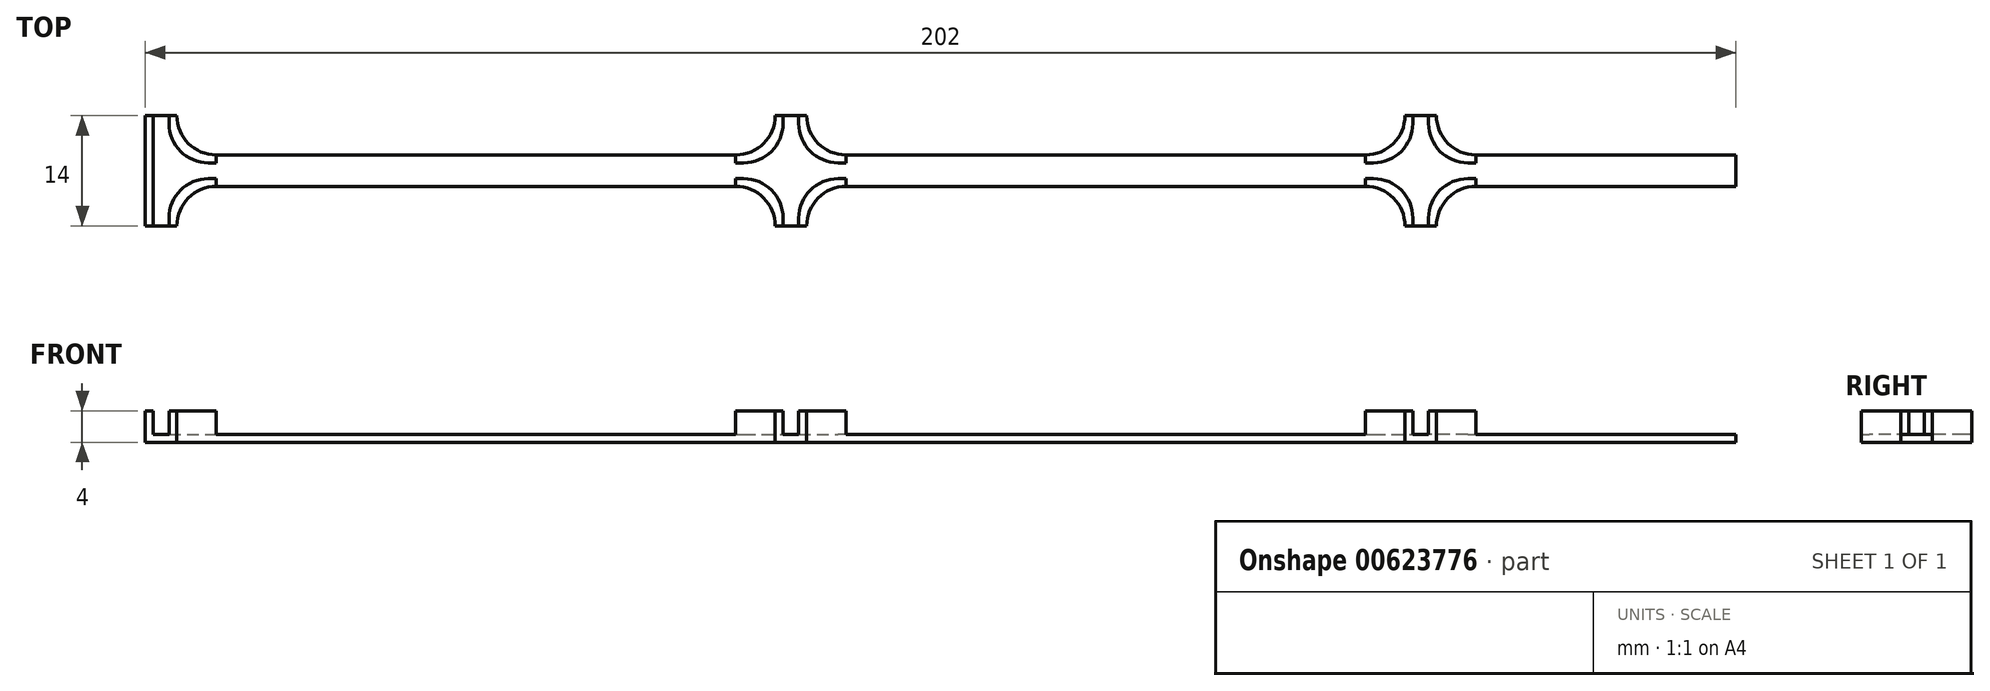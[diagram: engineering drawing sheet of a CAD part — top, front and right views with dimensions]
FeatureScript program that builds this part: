
annotation { "Feature Type Name" : "Feature", "Feature Type Description" : "" }
export const myFeature = defineFeature(function(context is Context, id is Id, definition is map)
    precondition{}
    {
        {
            var Q0;
            Q0=qCreatedBy(makeId("Top.planeOp"),FACE);
            var sketch = newSketch(context, id + "F0", { "sketchPlane" : qUnion([Q0])});
            skLineSegment(sketch, "E0.bottom", {"start": v(101, -2) * mm, "end": v(-101, -2) * mm});
            skLineSegment(sketch, "E0.top", {"start": v(101, 2) * mm, "end": v(-101, 2) * mm});
            skLineSegment(sketch, "E0.left", {"start": v(101, -2) * mm, "end": v(101, 2) * mm});
            skLineSegment(sketch, "E0.right", {"start": v(-101, -2) * mm, "end": v(-101, 2) * mm});
            skPoint(sketch, "E0.middle", {"position": v(0, 0) * mm});
            skLineSegment(sketch, "E1.bottom", {"start": v(-101, 7) * mm, "end": v(-97, 7) * mm});
            skLineSegment(sketch, "E1.top", {"start": v(-101, -7) * mm, "end": v(-97, -7) * mm});
            skLineSegment(sketch, "E1.left", {"start": v(-101, 7) * mm, "end": v(-101, -7) * mm});
            skLineSegment(sketch, "E1.right", {"start": v(-97, 7) * mm, "end": v(-97, -7) * mm});
            skLineSegment(sketch, "E2", {"start": v(-101, 0) * mm, "end": v(-101, 0) * mm});
            skLineSegment(sketch, "E3.bottom", {"start": v(-21, 7) * mm, "end": v(-17, 7) * mm});
            skLineSegment(sketch, "E3.top", {"start": v(-21, -7) * mm, "end": v(-17, -7) * mm});
            skLineSegment(sketch, "E3.left", {"start": v(-21, 7) * mm, "end": v(-21, -7) * mm});
            skLineSegment(sketch, "E3.right", {"start": v(-17, 7) * mm, "end": v(-17, -7) * mm});
            skPoint(sketch, "E3.middle", {"position": v(-19, 0) * mm});
            skLineSegment(sketch, "E4", {"start": v(-97, 4.56) * mm, "end": v(-17, 4.56) * mm});
            skLineSegment(sketch, "E5.bottom", {"start": v(63, 7) * mm, "end": v(59, 7) * mm});
            skLineSegment(sketch, "E5.top", {"start": v(63, -7) * mm, "end": v(59, -7) * mm});
            skLineSegment(sketch, "E5.left", {"start": v(63, 7) * mm, "end": v(63, -7) * mm});
            skLineSegment(sketch, "E5.right", {"start": v(59, 7) * mm, "end": v(59, -7) * mm});
            skPoint(sketch, "E5.middle", {"position": v(61, 0) * mm});
            skLineSegment(sketch, "E6", {"start": v(-17, 4.56) * mm, "end": v(63, 4.56) * mm});
            skSolve(sketch);
        }
        {
            var Q0;
            {var subQ3=sQuery(id+"F0.wireOp",EDGE,"E1.bottom");Q0=makeQuery(id+"F0.imprint","IMPRINT",FACE,{"disambiguationData":[TD([[makeQuery(id+"F0.imprint","IMPRINT",EDGE,{"derivedFrom":subQ3}),-1.0]])]});}
            var Q1;
            {var subQ0=sQuery(id+"F0.wireOp",EDGE,"E1.left");var subQ1=sQuery(id+"F0.wireOp",EDGE,"E0.bottom");var subQ2=makeQuery(id+"F0.imprint","INTERSECT",VERTEX,{"derivedFrom":[subQ1,subQ0]});Q1=makeQuery(id+"F0.imprint","IMPRINT",FACE,{"disambiguationData":[TD([[makeQuery(id+"F0.imprint","IMPRINT",EDGE,{"disambiguationData":[TD([[subQ2,1.0]])],"derivedFrom":subQ1}),-1.0]])]});}
            var Q2;
            {var subQ5=sQuery(id+"F0.wireOp",EDGE,"E1.top");Q2=makeQuery(id+"F0.imprint","IMPRINT",FACE,{"disambiguationData":[TD([[makeQuery(id+"F0.imprint","IMPRINT",EDGE,{"derivedFrom":subQ5}),1.0]])]});}
            var Q3;
            {var subQ0=sQuery(id+"F0.wireOp",EDGE,"E3.left");var subQ1=sQuery(id+"F0.wireOp",EDGE,"E0.bottom");var subQ2=makeQuery(id+"F0.imprint","INTERSECT",VERTEX,{"derivedFrom":[subQ1,subQ0]});Q3=makeQuery(id+"F0.imprint","IMPRINT",FACE,{"disambiguationData":[TD([[makeQuery(id+"F0.imprint","IMPRINT",EDGE,{"disambiguationData":[TD([[subQ2,-1.0]])],"derivedFrom":subQ1}),-1.0]])]});}
            var Q4;
            {var subQ0=sQuery(id+"F0.wireOp",EDGE,"E3.right");var subQ1=sQuery(id+"F0.wireOp",EDGE,"E0.top");var subQ2=makeQuery(id+"F0.imprint","INTERSECT",VERTEX,{"derivedFrom":[subQ1,subQ0]});Q4=makeQuery(id+"F0.imprint","IMPRINT",FACE,{"disambiguationData":[TD([[makeQuery(id+"F0.imprint","IMPRINT",EDGE,{"disambiguationData":[TD([[subQ2,-1.0]])],"derivedFrom":subQ1}),-1.0]])]});}
            var Q5;
            {var subQ0=sQuery(id+"F0.wireOp",EDGE,"E3.right");var subQ1=sQuery(id+"F0.wireOp",EDGE,"E0.bottom");var subQ2=makeQuery(id+"F0.imprint","INTERSECT",VERTEX,{"derivedFrom":[subQ1,subQ0]});Q5=makeQuery(id+"F0.imprint","IMPRINT",FACE,{"disambiguationData":[TD([[makeQuery(id+"F0.imprint","IMPRINT",EDGE,{"disambiguationData":[TD([[subQ2,-1.0]])],"derivedFrom":subQ1}),-1.0]])]});}
            var Q6;
            {var subQ5=sQuery(id+"F0.wireOp",EDGE,"E3.top");Q6=makeQuery(id+"F0.imprint","IMPRINT",FACE,{"disambiguationData":[TD([[makeQuery(id+"F0.imprint","IMPRINT",EDGE,{"derivedFrom":subQ5}),1.0]])]});}
            var Q7;
            {var subQ0=sQuery(id+"F0.wireOp",EDGE,"E3.bottom");Q7=makeQuery(id+"F0.imprint","IMPRINT",FACE,{"disambiguationData":[TD([[makeQuery(id+"F0.imprint","IMPRINT",EDGE,{"derivedFrom":subQ0}),-1.0]])]});}
            var Q8;
            {var subQ0=sQuery(id+"F0.wireOp",EDGE,"E5.right");var subQ1=sQuery(id+"F0.wireOp",EDGE,"E0.bottom");var subQ2=makeQuery(id+"F0.imprint","INTERSECT",VERTEX,{"derivedFrom":[subQ1,subQ0]});Q8=makeQuery(id+"F0.imprint","IMPRINT",FACE,{"disambiguationData":[TD([[makeQuery(id+"F0.imprint","IMPRINT",EDGE,{"disambiguationData":[TD([[subQ2,-1.0]])],"derivedFrom":subQ1}),-1.0]])]});}
            var Q9;
            {var subQ0=sQuery(id+"F0.wireOp",EDGE,"E5.bottom");Q9=makeQuery(id+"F0.imprint","IMPRINT",FACE,{"disambiguationData":[TD([[makeQuery(id+"F0.imprint","IMPRINT",EDGE,{"derivedFrom":subQ0}),1.0]])]});}
            var Q10;
            {var subQ0=sQuery(id+"F0.wireOp",EDGE,"E5.left");var subQ1=sQuery(id+"F0.wireOp",EDGE,"E0.top");var subQ2=makeQuery(id+"F0.imprint","INTERSECT",VERTEX,{"derivedFrom":[subQ1,subQ0]});Q10=makeQuery(id+"F0.imprint","IMPRINT",FACE,{"disambiguationData":[TD([[makeQuery(id+"F0.imprint","IMPRINT",EDGE,{"disambiguationData":[TD([[subQ2,-1.0]])],"derivedFrom":subQ1}),-1.0]])]});}
            var Q11;
            {var subQ5=sQuery(id+"F0.wireOp",EDGE,"E5.top");Q11=makeQuery(id+"F0.imprint","IMPRINT",FACE,{"disambiguationData":[TD([[makeQuery(id+"F0.imprint","IMPRINT",EDGE,{"derivedFrom":subQ5}),-1.0]])]});}
            var Q12;
            {var subQ0=sQuery(id+"F0.wireOp",EDGE,"E5.left");var subQ1=sQuery(id+"F0.wireOp",EDGE,"E0.bottom");var subQ2=makeQuery(id+"F0.imprint","INTERSECT",VERTEX,{"derivedFrom":[subQ1,subQ0]});Q12=makeQuery(id+"F0.imprint","IMPRINT",FACE,{"disambiguationData":[TD([[makeQuery(id+"F0.imprint","IMPRINT",EDGE,{"disambiguationData":[TD([[subQ2,-1.0]])],"derivedFrom":subQ1}),-1.0]])]});}
            var Q13;
            {var subQ0=sQuery(id+"F0.wireOp",EDGE,"E0.left");Q13=makeQuery(id+"F0.imprint","IMPRINT",FACE,{"disambiguationData":[TD([[makeQuery(id+"F0.imprint","IMPRINT",EDGE,{"derivedFrom":subQ0}),1.0]])]});}
            extrude(context, id + "F1", {"entities" : qUnion([Q0, Q1, Q2, Q3, Q4, Q5, Q6, Q7, Q8, Q9, Q10, Q11, Q12, Q13]), "depth" : 1 * mm, "offsetDistance" : 25 * mm});
        }
        {
            var Q0;
            Q0=makeQuery(id+"F1.opExtrude","CAP_FACE",FACE,{"disambiguationData":[OSD([sQuery(id+"F0.wireOp",EDGE,"E0.bottom"),sQuery(id+"F0.wireOp",EDGE,"E0.top"),sQuery(id+"F0.wireOp",EDGE,"E0.left"),sQuery(id+"F0.wireOp",EDGE,"E1.bottom"),sQuery(id+"F0.wireOp",EDGE,"E1.top"),sQuery(id+"F0.wireOp",EDGE,"E1.left"),sQuery(id+"F0.wireOp",EDGE,"E1.right"),sQuery(id+"F0.wireOp",EDGE,"E3.bottom"),sQuery(id+"F0.wireOp",EDGE,"E3.top"),sQuery(id+"F0.wireOp",EDGE,"E3.left"),sQuery(id+"F0.wireOp",EDGE,"E3.right"),sQuery(id+"F0.wireOp",EDGE,"E5.bottom"),sQuery(id+"F0.wireOp",EDGE,"E5.top"),sQuery(id+"F0.wireOp",EDGE,"E5.left"),sQuery(id+"F0.wireOp",EDGE,"E5.right")])],"isStart":false});
            var sketch = newSketch(context, id + "F2", { "sketchPlane" : qUnion([Q0])});
            skLineSegment(sketch, "E7.bottom", {"start": v(-101, 7) * mm, "end": v(-100, 7) * mm});
            skLineSegment(sketch, "E7.top", {"start": v(-101, -7) * mm, "end": v(-100, -7) * mm});
            skLineSegment(sketch, "E7.left", {"start": v(-101, 7) * mm, "end": v(-101, -7) * mm});
            skLineSegment(sketch, "E7.right", {"start": v(-100, 7) * mm, "end": v(-100, -7) * mm});
            skLineSegment(sketch, "E8.bottom", {"start": v(-97, 2) * mm, "end": v(-98, 2) * mm});
            skLineSegment(sketch, "E8.top", {"start": v(-97, 7) * mm, "end": v(-98, 7) * mm});
            skLineSegment(sketch, "E8.left", {"start": v(-97, 2) * mm, "end": v(-97, 7) * mm});
            skLineSegment(sketch, "E8.right", {"start": v(-98, 2) * mm, "end": v(-98, 7) * mm});
            skLineSegment(sketch, "E9.bottom", {"start": v(-97, -2) * mm, "end": v(-98, -2) * mm});
            skLineSegment(sketch, "E9.top", {"start": v(-97, -7) * mm, "end": v(-98, -7) * mm});
            skLineSegment(sketch, "E9.left", {"start": v(-97, -2) * mm, "end": v(-97, -7) * mm});
            skLineSegment(sketch, "E9.right", {"start": v(-98, -2) * mm, "end": v(-98, -7) * mm});
            skLineSegment(sketch, "E10.bottom", {"start": v(-98, -2) * mm, "end": v(-92, -2) * mm});
            skLineSegment(sketch, "E10.top", {"start": v(-98, -1) * mm, "end": v(-92, -1) * mm});
            skLineSegment(sketch, "E10.left", {"start": v(-98, -2) * mm, "end": v(-98, -1) * mm});
            skLineSegment(sketch, "E10.right", {"start": v(-92, -2) * mm, "end": v(-92, -1) * mm});
            skPoint(sketch, "E11.oppositeSnap0", {"position": v(-92, -1.5) * mm});
            skLineSegment(sketch, "E11.bottom", {"start": v(-98, 2) * mm, "end": v(-92, 2) * mm});
            skLineSegment(sketch, "E11.top", {"start": v(-98, 1) * mm, "end": v(-92, 1) * mm});
            skLineSegment(sketch, "E11.left", {"start": v(-98, 2) * mm, "end": v(-98, 1) * mm});
            skLineSegment(sketch, "E11.right", {"start": v(-92, 2) * mm, "end": v(-92, 1) * mm});
            skLineSegment(sketch, "E12.bottom", {"start": v(-21, 7) * mm, "end": v(-20, 7) * mm});
            skLineSegment(sketch, "E12.top", {"start": v(-21, 1) * mm, "end": v(-20, 1) * mm});
            skLineSegment(sketch, "E12.left", {"start": v(-21, 7) * mm, "end": v(-21, 1) * mm});
            skLineSegment(sketch, "E12.right", {"start": v(-20, 7) * mm, "end": v(-20, 1) * mm});
            skPoint(sketch, "E13.oppositeSnap0", {"position": v(-20.5, 1) * mm});
            skLineSegment(sketch, "E13.bottom", {"start": v(-17, 7) * mm, "end": v(-18, 7) * mm});
            skLineSegment(sketch, "E13.top", {"start": v(-17, 1) * mm, "end": v(-18, 1) * mm});
            skLineSegment(sketch, "E13.left", {"start": v(-17, 7) * mm, "end": v(-17, 1) * mm});
            skLineSegment(sketch, "E13.right", {"start": v(-18, 7) * mm, "end": v(-18, 1) * mm});
            skLineSegment(sketch, "E14.bottom", {"start": v(-17, 1) * mm, "end": v(-12, 1) * mm});
            skLineSegment(sketch, "E14.top", {"start": v(-17, 2) * mm, "end": v(-12, 2) * mm});
            skLineSegment(sketch, "E14.left", {"start": v(-17, 1) * mm, "end": v(-17, 2) * mm});
            skLineSegment(sketch, "E14.right", {"start": v(-12, 1) * mm, "end": v(-12, 2) * mm});
            skPoint(sketch, "E15.oppositeSnap0", {"position": v(-12, 1.5) * mm});
            skLineSegment(sketch, "E15.bottom", {"start": v(-17, -2) * mm, "end": v(-12, -2) * mm});
            skLineSegment(sketch, "E15.top", {"start": v(-17, -1) * mm, "end": v(-12, -1) * mm});
            skLineSegment(sketch, "E15.left", {"start": v(-17, -2) * mm, "end": v(-17, -1) * mm});
            skLineSegment(sketch, "E15.right", {"start": v(-12, -2) * mm, "end": v(-12, -1) * mm});
            skLineSegment(sketch, "E16.bottom", {"start": v(-17, -1) * mm, "end": v(-18, -1) * mm});
            skLineSegment(sketch, "E16.top", {"start": v(-17, -7) * mm, "end": v(-18, -7) * mm});
            skLineSegment(sketch, "E16.left", {"start": v(-17, -1) * mm, "end": v(-17, -7) * mm});
            skLineSegment(sketch, "E16.right", {"start": v(-18, -1) * mm, "end": v(-18, -7) * mm});
            skLineSegment(sketch, "E17.bottom", {"start": v(-21, -2) * mm, "end": v(-26, -2) * mm});
            skLineSegment(sketch, "E17.top", {"start": v(-21, -1) * mm, "end": v(-26, -1) * mm});
            skLineSegment(sketch, "E17.left", {"start": v(-21, -2) * mm, "end": v(-21, -1) * mm});
            skLineSegment(sketch, "E17.right", {"start": v(-26, -2) * mm, "end": v(-26, -1) * mm});
            skLineSegment(sketch, "E18.bottom", {"start": v(-21, -1) * mm, "end": v(-20, -1) * mm});
            skLineSegment(sketch, "E18.top", {"start": v(-21, -7) * mm, "end": v(-20, -7) * mm});
            skLineSegment(sketch, "E18.left", {"start": v(-21, -1) * mm, "end": v(-21, -7) * mm});
            skLineSegment(sketch, "E18.right", {"start": v(-20, -1) * mm, "end": v(-20, -7) * mm});
            skPoint(sketch, "E19.oppositeSnap0", {"position": v(-26, -1.5) * mm});
            skLineSegment(sketch, "E19.bottom", {"start": v(-21, 2) * mm, "end": v(-26, 2) * mm});
            skLineSegment(sketch, "E19.top", {"start": v(-21, 1) * mm, "end": v(-26, 1) * mm});
            skLineSegment(sketch, "E19.left", {"start": v(-21, 2) * mm, "end": v(-21, 1) * mm});
            skLineSegment(sketch, "E19.right", {"start": v(-26, 2) * mm, "end": v(-26, 1) * mm});
            skLineSegment(sketch, "E20.bottom", {"start": v(59, 7) * mm, "end": v(60, 7) * mm});
            skLineSegment(sketch, "E20.top", {"start": v(59, 1) * mm, "end": v(60, 1) * mm});
            skLineSegment(sketch, "E20.left", {"start": v(59, 7) * mm, "end": v(59, 1) * mm});
            skLineSegment(sketch, "E20.right", {"start": v(60, 7) * mm, "end": v(60, 1) * mm});
            skLineSegment(sketch, "E21.bottom", {"start": v(63, 7) * mm, "end": v(62, 7) * mm});
            skLineSegment(sketch, "E21.top", {"start": v(63, 1) * mm, "end": v(62, 1) * mm});
            skLineSegment(sketch, "E21.left", {"start": v(63, 7) * mm, "end": v(63, 1) * mm});
            skLineSegment(sketch, "E21.right", {"start": v(62, 7) * mm, "end": v(62, 1) * mm});
            skLineSegment(sketch, "E22.bottom", {"start": v(59, -7) * mm, "end": v(60, -7) * mm});
            skLineSegment(sketch, "E22.top", {"start": v(59, -1) * mm, "end": v(60, -1) * mm});
            skLineSegment(sketch, "E22.left", {"start": v(59, -7) * mm, "end": v(59, -1) * mm});
            skLineSegment(sketch, "E22.right", {"start": v(60, -7) * mm, "end": v(60, -1) * mm});
            skLineSegment(sketch, "E23.bottom", {"start": v(63, -7) * mm, "end": v(62, -7) * mm});
            skLineSegment(sketch, "E23.top", {"start": v(63, -1) * mm, "end": v(62, -1) * mm});
            skLineSegment(sketch, "E23.left", {"start": v(63, -7) * mm, "end": v(63, -1) * mm});
            skLineSegment(sketch, "E23.right", {"start": v(62, -7) * mm, "end": v(62, -1) * mm});
            skLineSegment(sketch, "E24.bottom", {"start": v(63, -1) * mm, "end": v(68, -1) * mm});
            skLineSegment(sketch, "E24.top", {"start": v(63, -2) * mm, "end": v(68, -2) * mm});
            skLineSegment(sketch, "E24.left", {"start": v(63, -1) * mm, "end": v(63, -2) * mm});
            skLineSegment(sketch, "E24.right", {"start": v(68, -1) * mm, "end": v(68, -2) * mm});
            skLineSegment(sketch, "E25.bottom", {"start": v(63, 1) * mm, "end": v(68, 1) * mm});
            skLineSegment(sketch, "E25.top", {"start": v(63, 2) * mm, "end": v(68, 2) * mm});
            skLineSegment(sketch, "E25.left", {"start": v(63, 1) * mm, "end": v(63, 2) * mm});
            skLineSegment(sketch, "E25.right", {"start": v(68, 1) * mm, "end": v(68, 2) * mm});
            skLineSegment(sketch, "E26.bottom", {"start": v(59, -1) * mm, "end": v(54, -1) * mm});
            skLineSegment(sketch, "E26.top", {"start": v(59, -2) * mm, "end": v(54, -2) * mm});
            skLineSegment(sketch, "E26.left", {"start": v(59, -1) * mm, "end": v(59, -2) * mm});
            skLineSegment(sketch, "E26.right", {"start": v(54, -1) * mm, "end": v(54, -2) * mm});
            skLineSegment(sketch, "E27.bottom", {"start": v(59, 1) * mm, "end": v(54, 1) * mm});
            skLineSegment(sketch, "E27.top", {"start": v(59, 2) * mm, "end": v(54, 2) * mm});
            skLineSegment(sketch, "E27.left", {"start": v(59, 1) * mm, "end": v(59, 2) * mm});
            skLineSegment(sketch, "E27.right", {"start": v(54, 1) * mm, "end": v(54, 2) * mm});
            skSolve(sketch);
        }
        {
            var Q0;
            Q0=makeQuery(id+"F2.imprint","IMPRINT",FACE,{"disambiguationData":[TD([[makeQuery(id+"F2.imprint","IMPRINT",EDGE,{"derivedFrom":sQuery(id+"F2.wireOp",EDGE,"E7.bottom")}),-1.0]])]});
            var Q1;
            Q1=makeQuery(id+"F2.imprint","IMPRINT",FACE,{"disambiguationData":[TD([[makeQuery(id+"F2.imprint","IMPRINT",EDGE,{"derivedFrom":sQuery(id+"F2.wireOp",EDGE,"E8.top")}),-1.0]])]});
            var Q2;
            Q2=makeQuery(id+"F2.imprint","IMPRINT",FACE,{"disambiguationData":[TD([[makeQuery(id+"F2.imprint","IMPRINT",EDGE,{"derivedFrom":sQuery(id+"F2.wireOp",EDGE,"E11.top")}),1.0]])]});
            var Q3;
            Q3=makeQuery(id+"F2.imprint","IMPRINT",FACE,{"disambiguationData":[TD([[makeQuery(id+"F2.imprint","IMPRINT",EDGE,{"derivedFrom":sQuery(id+"F2.wireOp",EDGE,"E10.top")}),-1.0]])]});
            var Q4;
            Q4=makeQuery(id+"F2.imprint","IMPRINT",FACE,{"disambiguationData":[TD([[makeQuery(id+"F2.imprint","IMPRINT",EDGE,{"derivedFrom":sQuery(id+"F2.wireOp",EDGE,"E9.top")}),1.0]])]});
            extrude(context, id + "F3", {"entities" : qUnion([Q0, Q1, Q2, Q3, Q4]), "operationType" : NewBodyOperationType.ADD, "depth" : 3 * mm, "offsetDistance" : 25 * mm});
        }
        {
            var Q0;
            Q0=makeQuery(id+"F3.boolean.opBoolean","MERGE",EDGE,{"derivedFrom":[makeQuery(id+"F1.opExtrude","SWEPT_EDGE",EDGE,{"disambiguationData":[OSD([sQuery(id+"F0.wireOp",EDGE,"E0.bottom"),sQuery(id+"F0.wireOp",EDGE,"E1.right")])]}),makeQuery(id+"F3.opExtrude","SWEPT_EDGE",EDGE,{"disambiguationData":[OSD([sQuery(id+"F2.wireOp",EDGE,"E9.left"),sQuery(id+"F2.wireOp",EDGE,"E10.bottom")])]})]});
            var Q1;
            Q1=makeQuery(id+"F3.opExtrude","SWEPT_EDGE",EDGE,{"disambiguationData":[OSD([sQuery(id+"F2.wireOp",EDGE,"E11.top"),sQuery(id+"F2.wireOp",EDGE,"E11.left")])]});
            var Q2;
            Q2=makeQuery(id+"F3.opExtrude","SWEPT_EDGE",EDGE,{"disambiguationData":[OSD([sQuery(id+"F2.wireOp",EDGE,"E10.top"),sQuery(id+"F2.wireOp",EDGE,"E10.left")])]});
            var Q3;
            Q3=makeQuery(id+"F3.boolean.opBoolean","MERGE",EDGE,{"derivedFrom":[makeQuery(id+"F1.opExtrude","SWEPT_EDGE",EDGE,{"disambiguationData":[OSD([sQuery(id+"F0.wireOp",EDGE,"E0.top"),sQuery(id+"F0.wireOp",EDGE,"E1.right")])]}),makeQuery(id+"F3.opExtrude","SWEPT_EDGE",EDGE,{"disambiguationData":[OSD([sQuery(id+"F2.wireOp",EDGE,"E8.left"),sQuery(id+"F2.wireOp",EDGE,"E11.bottom")])]})]});
            fillet(context, id + "F4", {"entities" : qUnion([Q0, Q1, Q2, Q3]), "radius" : 5 * mm, "tangentPropagation" : true, "allowEdgeOverflow" : false});
        }
        {
            var Q0;
            Q0=makeQuery(id+"F2.imprint","IMPRINT",FACE,{"disambiguationData":[TD([[makeQuery(id+"F2.imprint","IMPRINT",EDGE,{"derivedFrom":sQuery(id+"F2.wireOp",EDGE,"E12.bottom")}),-1.0]])]});
            var Q1;
            Q1=makeQuery(id+"F2.imprint","IMPRINT",FACE,{"disambiguationData":[TD([[makeQuery(id+"F2.imprint","IMPRINT",EDGE,{"derivedFrom":sQuery(id+"F2.wireOp",EDGE,"E13.bottom")}),-1.0]])]});
            var Q2;
            Q2=makeQuery(id+"F2.imprint","IMPRINT",FACE,{"disambiguationData":[TD([[makeQuery(id+"F2.imprint","IMPRINT",EDGE,{"derivedFrom":sQuery(id+"F2.wireOp",EDGE,"E14.bottom")}),1.0]])]});
            var Q3;
            Q3=makeQuery(id+"F2.imprint","IMPRINT",FACE,{"disambiguationData":[TD([[makeQuery(id+"F2.imprint","IMPRINT",EDGE,{"derivedFrom":sQuery(id+"F2.wireOp",EDGE,"E19.bottom")}),1.0]])]});
            var Q4;
            {var subQ0=sQuery(id+"F2.wireOp",EDGE,"E17.bottom");Q4=makeQuery(id+"F2.imprint","IMPRINT",FACE,{"disambiguationData":[TD([[makeQuery(id+"F2.imprint","IMPRINT",EDGE,{"derivedFrom":subQ0}),-1.0]])]});}
            var Q5;
            {var subQ3=sQuery(id+"F2.wireOp",EDGE,"E18.bottom");Q5=makeQuery(id+"F2.imprint","IMPRINT",FACE,{"disambiguationData":[TD([[makeQuery(id+"F2.imprint","IMPRINT",EDGE,{"derivedFrom":subQ3}),-1.0]])]});}
            var Q6;
            {var subQ0=sQuery(id+"F2.wireOp",EDGE,"E15.bottom");Q6=makeQuery(id+"F2.imprint","IMPRINT",FACE,{"disambiguationData":[TD([[makeQuery(id+"F2.imprint","IMPRINT",EDGE,{"derivedFrom":subQ0}),-1.0]])]});}
            var Q7;
            {var subQ3=sQuery(id+"F2.wireOp",EDGE,"E16.bottom");Q7=makeQuery(id+"F2.imprint","IMPRINT",FACE,{"disambiguationData":[TD([[makeQuery(id+"F2.imprint","IMPRINT",EDGE,{"derivedFrom":subQ3}),1.0]])]});}
            extrude(context, id + "F5", {"entities" : qUnion([Q0, Q1, Q2, Q3, Q4, Q5, Q6, Q7]), "operationType" : NewBodyOperationType.ADD, "depth" : 3 * mm, "offsetDistance" : 25 * mm});
        }
        {
            var Q0;
            Q0=makeQuery(id+"F5.opExtrude","SWEPT_EDGE",EDGE,{"disambiguationData":[OSD([sQuery(id+"F2.wireOp",EDGE,"E13.top"),sQuery(id+"F2.wireOp",EDGE,"E13.right")])]});
            var Q1;
            Q1=makeQuery(id+"F5.opExtrude","SWEPT_EDGE",EDGE,{"disambiguationData":[OSD([sQuery(id+"F2.wireOp",EDGE,"E12.top"),sQuery(id+"F2.wireOp",EDGE,"E12.right")])]});
            var Q2;
            Q2=makeQuery(id+"F5.boolean.opBoolean","MERGE",EDGE,{"derivedFrom":[makeQuery(id+"F1.opExtrude","SWEPT_EDGE",EDGE,{"disambiguationData":[OSD([sQuery(id+"F0.wireOp",EDGE,"E0.bottom"),sQuery(id+"F0.wireOp",EDGE,"E3.right")])]}),makeQuery(id+"F5.opExtrude","SWEPT_EDGE",EDGE,{"disambiguationData":[OSD([sQuery(id+"F2.wireOp",EDGE,"E15.bottom"),sQuery(id+"F2.wireOp",EDGE,"E16.left")])]})]});
            var Q3;
            Q3=makeQuery(id+"F5.opExtrude","SWEPT_EDGE",EDGE,{"disambiguationData":[OSD([sQuery(id+"F2.wireOp",EDGE,"E18.bottom"),sQuery(id+"F2.wireOp",EDGE,"E18.right")])]});
            var Q4;
            Q4=makeQuery(id+"F5.boolean.opBoolean","MERGE",EDGE,{"derivedFrom":[makeQuery(id+"F1.opExtrude","SWEPT_EDGE",EDGE,{"disambiguationData":[OSD([sQuery(id+"F0.wireOp",EDGE,"E0.bottom"),sQuery(id+"F0.wireOp",EDGE,"E3.left")])]}),makeQuery(id+"F5.opExtrude","SWEPT_EDGE",EDGE,{"disambiguationData":[OSD([sQuery(id+"F2.wireOp",EDGE,"E17.bottom"),sQuery(id+"F2.wireOp",EDGE,"E18.left")])]})]});
            var Q5;
            Q5=makeQuery(id+"F5.boolean.opBoolean","MERGE",EDGE,{"derivedFrom":[makeQuery(id+"F1.opExtrude","SWEPT_EDGE",EDGE,{"disambiguationData":[OSD([sQuery(id+"F0.wireOp",EDGE,"E0.top"),sQuery(id+"F0.wireOp",EDGE,"E3.left")])]}),makeQuery(id+"F5.opExtrude","SWEPT_EDGE",EDGE,{"disambiguationData":[OSD([sQuery(id+"F2.wireOp",EDGE,"E12.left"),sQuery(id+"F2.wireOp",EDGE,"E19.bottom"),sQuery(id+"F2.wireOp",EDGE,"E19.left")])]})]});
            var Q6;
            Q6=makeQuery(id+"F5.boolean.opBoolean","MERGE",EDGE,{"derivedFrom":[makeQuery(id+"F1.opExtrude","SWEPT_EDGE",EDGE,{"disambiguationData":[OSD([sQuery(id+"F0.wireOp",EDGE,"E0.top"),sQuery(id+"F0.wireOp",EDGE,"E3.right")])]}),makeQuery(id+"F5.opExtrude","SWEPT_EDGE",EDGE,{"disambiguationData":[OSD([sQuery(id+"F2.wireOp",EDGE,"E13.left"),sQuery(id+"F2.wireOp",EDGE,"E14.top"),sQuery(id+"F2.wireOp",EDGE,"E14.left")])]})]});
            var Q7;
            Q7=makeQuery(id+"F5.opExtrude","SWEPT_EDGE",EDGE,{"disambiguationData":[OSD([sQuery(id+"F2.wireOp",EDGE,"E16.bottom"),sQuery(id+"F2.wireOp",EDGE,"E16.right")])]});
            fillet(context, id + "F6", {"entities" : qUnion([Q0, Q1, Q2, Q3, Q4, Q5, Q6, Q7]), "radius" : 5 * mm, "tangentPropagation" : true, "allowEdgeOverflow" : false});
        }
        {
            var Q0;
            Q0=makeQuery(id+"F2.imprint","IMPRINT",FACE,{"disambiguationData":[TD([[makeQuery(id+"F2.imprint","IMPRINT",EDGE,{"derivedFrom":sQuery(id+"F2.wireOp",EDGE,"E20.bottom")}),1.0]])]});
            var Q1;
            Q1=makeQuery(id+"F2.imprint","IMPRINT",FACE,{"disambiguationData":[TD([[makeQuery(id+"F2.imprint","IMPRINT",EDGE,{"derivedFrom":sQuery(id+"F2.wireOp",EDGE,"E25.bottom")}),1.0]])]});
            var Q2;
            Q2=makeQuery(id+"F2.imprint","IMPRINT",FACE,{"disambiguationData":[TD([[makeQuery(id+"F2.imprint","IMPRINT",EDGE,{"derivedFrom":sQuery(id+"F2.wireOp",EDGE,"E21.bottom")}),1.0]])]});
            var Q3;
            Q3=makeQuery(id+"F2.imprint","IMPRINT",FACE,{"disambiguationData":[TD([[makeQuery(id+"F2.imprint","IMPRINT",EDGE,{"derivedFrom":sQuery(id+"F2.wireOp",EDGE,"E24.bottom")}),-1.0]])]});
            var Q4;
            Q4=makeQuery(id+"F2.imprint","IMPRINT",FACE,{"disambiguationData":[TD([[makeQuery(id+"F2.imprint","IMPRINT",EDGE,{"derivedFrom":sQuery(id+"F2.wireOp",EDGE,"E23.bottom")}),-1.0]])]});
            var Q5;
            Q5=makeQuery(id+"F2.imprint","IMPRINT",FACE,{"disambiguationData":[TD([[makeQuery(id+"F2.imprint","IMPRINT",EDGE,{"derivedFrom":sQuery(id+"F2.wireOp",EDGE,"E27.bottom")}),-1.0]])]});
            var Q6;
            Q6=makeQuery(id+"F2.imprint","IMPRINT",FACE,{"disambiguationData":[TD([[makeQuery(id+"F2.imprint","IMPRINT",EDGE,{"derivedFrom":sQuery(id+"F2.wireOp",EDGE,"E26.bottom")}),1.0]])]});
            var Q7;
            Q7=makeQuery(id+"F2.imprint","IMPRINT",FACE,{"disambiguationData":[TD([[makeQuery(id+"F2.imprint","IMPRINT",EDGE,{"derivedFrom":sQuery(id+"F2.wireOp",EDGE,"E22.bottom")}),-1.0]])]});
            extrude(context, id + "F7", {"entities" : qUnion([Q0, Q1, Q2, Q3, Q4, Q5, Q6, Q7]), "operationType" : NewBodyOperationType.ADD, "depth" : 3 * mm, "offsetDistance" : 25 * mm});
        }
        {
            var Q0;
            Q0=makeQuery(id+"F7.boolean.opBoolean","MERGE",EDGE,{"derivedFrom":[makeQuery(id+"F1.opExtrude","SWEPT_EDGE",EDGE,{"disambiguationData":[OSD([sQuery(id+"F0.wireOp",EDGE,"E0.bottom"),sQuery(id+"F0.wireOp",EDGE,"E5.left")])]}),makeQuery(id+"F7.opExtrude","SWEPT_EDGE",EDGE,{"disambiguationData":[OSD([sQuery(id+"F2.wireOp",EDGE,"E23.left"),sQuery(id+"F2.wireOp",EDGE,"E24.top"),sQuery(id+"F2.wireOp",EDGE,"E24.left")])]})]});
            var Q1;
            Q1=makeQuery(id+"F7.opExtrude","SWEPT_EDGE",EDGE,{"disambiguationData":[OSD([sQuery(id+"F2.wireOp",EDGE,"E20.top"),sQuery(id+"F2.wireOp",EDGE,"E20.right")])]});
            var Q2;
            Q2=makeQuery(id+"F7.opExtrude","SWEPT_EDGE",EDGE,{"disambiguationData":[OSD([sQuery(id+"F2.wireOp",EDGE,"E21.top"),sQuery(id+"F2.wireOp",EDGE,"E21.right")])]});
            var Q3;
            Q3=makeQuery(id+"F7.opExtrude","SWEPT_EDGE",EDGE,{"disambiguationData":[OSD([sQuery(id+"F2.wireOp",EDGE,"E22.top"),sQuery(id+"F2.wireOp",EDGE,"E22.right")])]});
            var Q4;
            Q4=makeQuery(id+"F7.opExtrude","SWEPT_EDGE",EDGE,{"disambiguationData":[OSD([sQuery(id+"F2.wireOp",EDGE,"E23.top"),sQuery(id+"F2.wireOp",EDGE,"E23.right")])]});
            var Q5;
            Q5=makeQuery(id+"F7.boolean.opBoolean","MERGE",EDGE,{"derivedFrom":[makeQuery(id+"F1.opExtrude","SWEPT_EDGE",EDGE,{"disambiguationData":[OSD([sQuery(id+"F0.wireOp",EDGE,"E0.bottom"),sQuery(id+"F0.wireOp",EDGE,"E5.right")])]}),makeQuery(id+"F7.opExtrude","SWEPT_EDGE",EDGE,{"disambiguationData":[OSD([sQuery(id+"F2.wireOp",EDGE,"E22.left"),sQuery(id+"F2.wireOp",EDGE,"E26.top"),sQuery(id+"F2.wireOp",EDGE,"E26.left")])]})]});
            var Q6;
            Q6=makeQuery(id+"F7.boolean.opBoolean","MERGE",EDGE,{"derivedFrom":[makeQuery(id+"F1.opExtrude","SWEPT_EDGE",EDGE,{"disambiguationData":[OSD([sQuery(id+"F0.wireOp",EDGE,"E0.top"),sQuery(id+"F0.wireOp",EDGE,"E5.right")])]}),makeQuery(id+"F7.opExtrude","SWEPT_EDGE",EDGE,{"disambiguationData":[OSD([sQuery(id+"F2.wireOp",EDGE,"E20.left"),sQuery(id+"F2.wireOp",EDGE,"E27.top"),sQuery(id+"F2.wireOp",EDGE,"E27.left")])]})]});
            var Q7;
            Q7=makeQuery(id+"F7.boolean.opBoolean","MERGE",EDGE,{"derivedFrom":[makeQuery(id+"F1.opExtrude","SWEPT_EDGE",EDGE,{"disambiguationData":[OSD([sQuery(id+"F0.wireOp",EDGE,"E0.top"),sQuery(id+"F0.wireOp",EDGE,"E5.left")])]}),makeQuery(id+"F7.opExtrude","SWEPT_EDGE",EDGE,{"disambiguationData":[OSD([sQuery(id+"F2.wireOp",EDGE,"E21.left"),sQuery(id+"F2.wireOp",EDGE,"E25.top"),sQuery(id+"F2.wireOp",EDGE,"E25.left")])]})]});
            fillet(context, id + "F8", {"entities" : qUnion([Q0, Q1, Q2, Q3, Q4, Q5, Q6, Q7]), "radius" : 5 * mm, "tangentPropagation" : true, "allowEdgeOverflow" : false});
        }
    });
